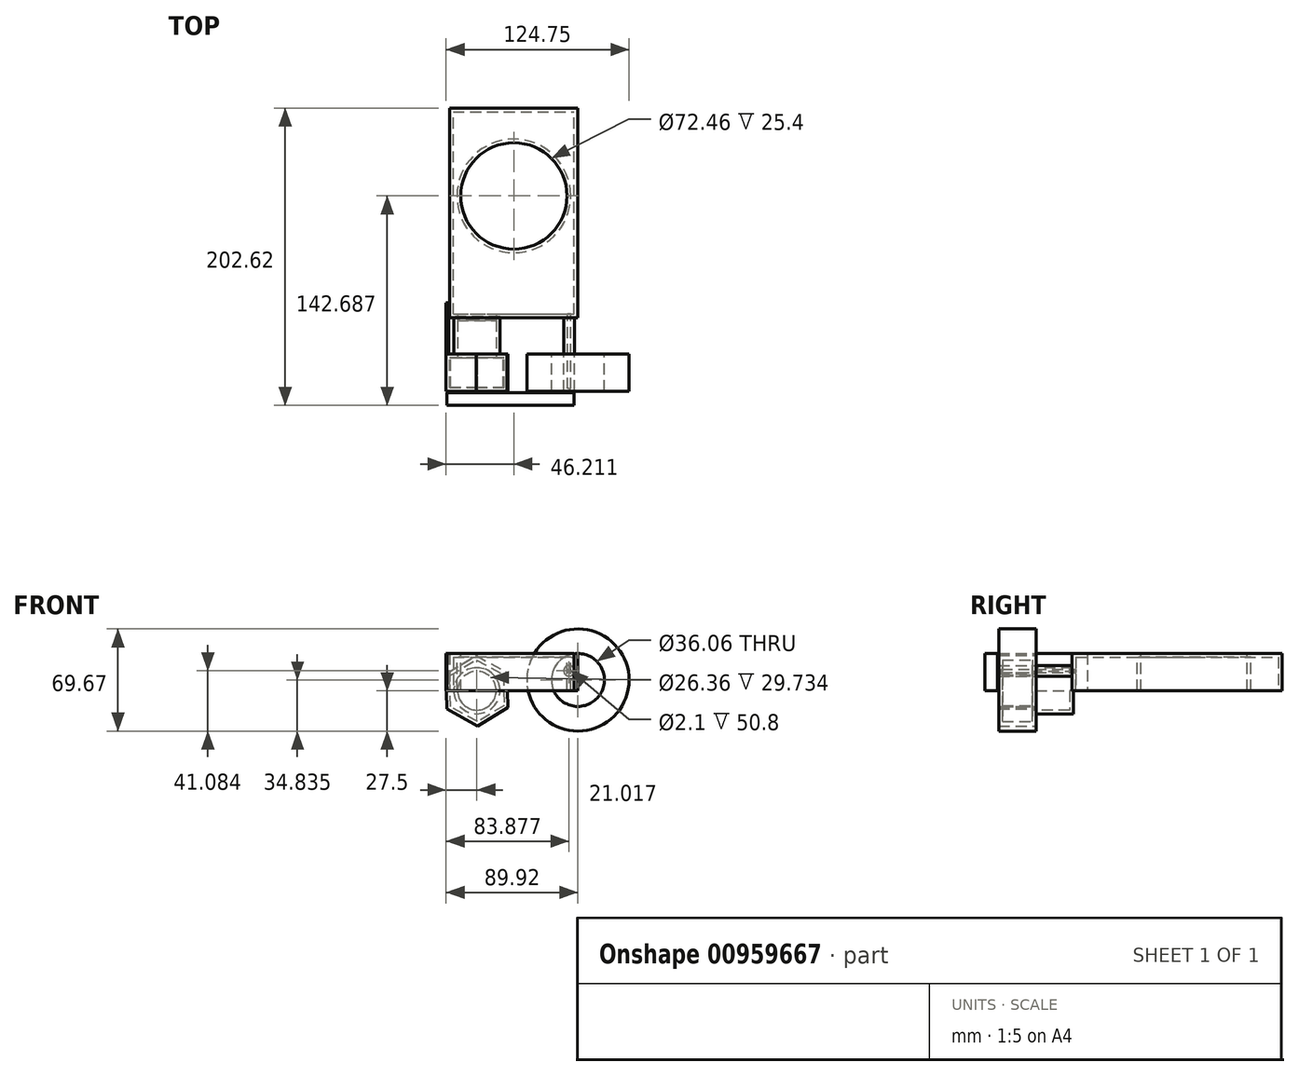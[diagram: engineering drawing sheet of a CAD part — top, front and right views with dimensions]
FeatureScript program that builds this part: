
annotation { "Feature Type Name" : "Feature", "Feature Type Description" : "" }
export const myFeature = defineFeature(function(context is Context, id is Id, definition is map)
    precondition{}
    {
        {
            var Q0;
            Q0=qCreatedBy(makeId("Front.planeOp"),FACE);
            var sketch = newSketch(context, id + "F0", { "sketchPlane" : qUnion([Q0])});
            skCircle(sketch, "E0.cCircle", {"center": v(-68.87, 0) * mm, "radius": 24 * mm, "construction": true});
            skLineSegment(sketch, "E0.0", {"start": v(-69.42, 23.98) * mm, "end": v(-48.38, 12.47) * mm});
            skLineSegment(sketch, "E0.1", {"start": v(-48.38, 12.47) * mm, "end": v(-47.83, -11.52) * mm});
            skLineSegment(sketch, "E0.2", {"start": v(-47.83, -11.52) * mm, "end": v(-68.32, -23.98) * mm});
            skLineSegment(sketch, "E0.3", {"start": v(-68.32, -23.98) * mm, "end": v(-89.37, -12.47) * mm});
            skLineSegment(sketch, "E0.4", {"start": v(-89.37, -12.47) * mm, "end": v(-89.92, 11.52) * mm});
            skLineSegment(sketch, "E0.5", {"start": v(-89.92, 11.52) * mm, "end": v(-69.42, 23.98) * mm});
            skSolve(sketch);
        }
        {
            var Q0;
            Q0=makeQuery(id+"F0.imprint","IMPRINT",FACE,{"disambiguationData":[TD([[makeQuery(id+"F0.imprint","IMPRINT",EDGE,{"derivedFrom":sQuery(id+"F0.wireOp",EDGE,"E0.0")}),-1.0]])]});
            extrude(context, id + "F1", {"entities" : qUnion([Q0]), "depth" : 25.4 * mm, "offsetDistance" : 25.4 * mm});
        }
        {
            var Q0;
            Q0=qCreatedBy(makeId("Front.planeOp"),FACE);
            var sketch = newSketch(context, id + "F2", { "sketchPlane" : qUnion([Q0])});
            skCircle(sketch, "E1", {"center": v(0, 0) * mm, "radius": 25.9 * mm});
            skCircle(sketch, "E2", {"center": v(0, 0) * mm, "radius": 17.2 * mm});
            skSolve(sketch);
        }
        {
            var Q0;
            Q0=makeQuery(id+"F2.imprint","IMPRINT",FACE,{"disambiguationData":[TD([[makeQuery(id+"F2.imprint","IMPRINT",EDGE,{"derivedFrom":sQuery(id+"F2.wireOp",EDGE,"E2")}),1.0]])]});
            var Q1;
            Q1=makeQuery(id+"F2.imprint","IMPRINT",FACE,{"disambiguationData":[TD([[makeQuery(id+"F2.imprint","IMPRINT",EDGE,{"derivedFrom":sQuery(id+"F2.wireOp",EDGE,"E1")}),1.0]])]});
            extrude(context, id + "F3", {"entities" : qUnion([Q0, Q1]), "operationType" : NewBodyOperationType.REMOVE, "oppositeDirection" : true, "depth" : 25.4 * mm, "offsetDistance" : 25.4 * mm});
        }
        {
            var Q0;
            Q0=qCreatedBy(makeId("Front.planeOp"),FACE);
            var sketch = newSketch(context, id + "F4", { "sketchPlane" : qUnion([Q0])});
            skCircle(sketch, "E3", {"center": v(0, 7.34) * mm, "radius": 34.83 * mm});
            skCircle(sketch, "E4", {"center": v(0, 7.34) * mm, "radius": 18.03 * mm});
            skSolve(sketch);
        }
        {
            var Q0;
            Q0 = qSketchRegion(id + "F4", true);
            extrude(context, id + "F5", {"entities" : qUnion([Q0]), "depth" : 25.4 * mm, "offsetDistance" : 25.4 * mm});
        }
        {
            var Q0;
            Q0=qCreatedBy(makeId("Front.planeOp"),FACE);
            var sketch = newSketch(context, id + "F6", { "sketchPlane" : qUnion([Q0])});
            skCircle(sketch, "E5", {"center": v(-68.46, 0) * mm, "radius": 14.96 * mm});
            skSolve(sketch);
        }
        {
            var Q0;
            Q0=makeQuery(id+"F6.imprint","IMPRINT",FACE,{"disambiguationData":[TD([[makeQuery(id+"F6.imprint","IMPRINT",EDGE,{"derivedFrom":sQuery(id+"F6.wireOp",EDGE,"E5")}),1.0]])]});
            extrude(context, id + "F7", {"entities" : qUnion([Q0]), "operationType" : NewBodyOperationType.ADD, "depth" : 25.4 * mm, "offsetDistance" : 25.4 * mm});
        }
        {
            var Q0;
            Q0=makeQuery(id+"F1.opExtrude","CAP_FACE",FACE,{"disambiguationData":[OSD([sQuery(id+"F0.wireOp",EDGE,"E0.0"),sQuery(id+"F0.wireOp",EDGE,"E0.1"),sQuery(id+"F0.wireOp",EDGE,"E0.2"),sQuery(id+"F0.wireOp",EDGE,"E0.3"),sQuery(id+"F0.wireOp",EDGE,"E0.4"),sQuery(id+"F0.wireOp",EDGE,"E0.5")])],"isStart":true});
            var sketch = newSketch(context, id + "F8", { "sketchPlane" : qUnion([Q0])});
            skCircle(sketch, "E6", {"center": v(68.9, 0) * mm, "radius": 15.72 * mm});
            skSolve(sketch);
        }
        {
            var Q0;
            Q0=makeQuery(id+"F8.imprint","IMPRINT",FACE,{"disambiguationData":[TD([[makeQuery(id+"F8.imprint","IMPRINT",EDGE,{"derivedFrom":sQuery(id+"F8.wireOp",EDGE,"E6")}),1.0]])]});
            extrude(context, id + "F9", {"entities" : qUnion([Q0]), "operationType" : NewBodyOperationType.ADD, "depth" : 25.4 * mm, "offsetDistance" : 25.4 * mm});
        }
        {
            var Q0;
            Q0=qCreatedBy(makeId("Top.planeOp"),FACE);
            var sketch = newSketch(context, id + "F10", { "sketchPlane" : qUnion([Q0])});
            skLineSegment(sketch, "E7.bottom", {"start": v(-87.54, 24.65) * mm, "end": v(0, 24.65) * mm});
            skLineSegment(sketch, "E7.top", {"start": v(-87.54, 38.16) * mm, "end": v(0, 38.16) * mm});
            skLineSegment(sketch, "E7.left", {"start": v(-87.54, 24.65) * mm, "end": v(-87.54, 38.16) * mm});
            skLineSegment(sketch, "E7.right", {"start": v(0, 24.65) * mm, "end": v(0, 38.16) * mm});
            skSolve(sketch);
        }
        {
            var Q0;
            Q0 = qSketchRegion(id + "F10", true);
            extrude(context, id + "F11", {"entities" : qUnion([Q0]), "operationType" : NewBodyOperationType.ADD, "depth" : 25.4 * mm, "offsetDistance" : 25.4 * mm});
        }
        {
            var Q0;
            Q0=makeQuery(id+"F11.opExtrude","SWEPT_FACE",FACE,{"disambiguationData":[OSD([sQuery(id+"F10.wireOp",EDGE,"E7.bottom")])]});
            var sketch = newSketch(context, id + "F12", { "sketchPlane" : qUnion([Q0])});
            skCircle(sketch, "E8", {"center": v(-6.04, 13.58) * mm, "radius": 3.59 * mm});
            skSolve(sketch);
        }
        {
            var Q0;
            Q0=makeQuery(id+"F12.imprint","IMPRINT",FACE,{"disambiguationData":[TD([[makeQuery(id+"F12.imprint","IMPRINT",EDGE,{"derivedFrom":sQuery(id+"F12.wireOp",EDGE,"E8")}),1.0]])]});
            extrude(context, id + "F13", {"entities" : qUnion([Q0]), "operationType" : NewBodyOperationType.ADD, "depth" : 25.4 * mm, "offsetDistance" : 25.4 * mm});
        }
        {
            var Q0;
            Q0=makeQuery(id+"F11.opExtrude","SWEPT_FACE",FACE,{"disambiguationData":[OSD([sQuery(id+"F10.wireOp",EDGE,"E7.top")])]});
            var sketch = newSketch(context, id + "F14", { "sketchPlane" : qUnion([Q0])});
            skLineSegment(sketch, "E9.bottom", {"start": v(87.54, 0) * mm, "end": v(49.94, 0) * mm});
            skLineSegment(sketch, "E9.top", {"start": v(87.54, -17.9) * mm, "end": v(49.94, -17.9) * mm});
            skLineSegment(sketch, "E9.left", {"start": v(87.54, 0) * mm, "end": v(87.54, -17.9) * mm});
            skLineSegment(sketch, "E9.right", {"start": v(49.94, 0) * mm, "end": v(49.94, -17.9) * mm});
            skSolve(sketch);
        }
        {
            var Q0;
            {var subQ3=sQuery(id+"F14.wireOp",EDGE,"E9.bottom");Q0=makeQuery(id+"F14.imprint","IMPRINT",FACE,{"disambiguationData":[TD([[makeQuery(id+"F14.imprint","IMPRINT",EDGE,{"derivedFrom":subQ3}),-1.0]])]});}
            extrude(context, id + "F15", {"entities" : qUnion([Q0]), "operationType" : NewBodyOperationType.ADD, "depth" : 129.54 * mm, "offsetDistance" : 25.4 * mm});
        }
        {
            var Q0;
            Q0=makeQuery(id+"F13.opExtrude","CAP_FACE",FACE,{"disambiguationData":[OSD([sQuery(id+"F12.wireOp",EDGE,"E8")])],"isStart":false});
            extrude(context, id + "F16", {"entities" : qUnion([Q0]), "operationType" : NewBodyOperationType.ADD, "depth" : 25.4 * mm, "offsetDistance" : 25.4 * mm});
        }
        {
            var Q0;
            Q0=qCreatedBy(makeId("Top.planeOp"),FACE);
            var sketch = newSketch(context, id + "F17", { "sketchPlane" : qUnion([Q0])});
            skLineSegment(sketch, "E10.bottom", {"start": v(-2.6, -26.22) * mm, "end": v(-2.6, -26.22) * mm});
            skLineSegment(sketch, "E10.top", {"start": v(-2.6, -25.99) * mm, "end": v(-2.6, -25.99) * mm});
            skLineSegment(sketch, "E10.left", {"start": v(-2.6, -26.22) * mm, "end": v(-2.6, -25.99) * mm});
            skLineSegment(sketch, "E10.right", {"start": v(-2.6, -26.22) * mm, "end": v(-2.6, -25.99) * mm});
            skLineSegment(sketch, "E11.bottom", {"start": v(-2.6, -26.22) * mm, "end": v(-89.4, -26.22) * mm});
            skLineSegment(sketch, "E11.top", {"start": v(-2.6, -34.92) * mm, "end": v(-89.4, -34.92) * mm});
            skLineSegment(sketch, "E11.left", {"start": v(-2.6, -26.22) * mm, "end": v(-2.6, -34.92) * mm});
            skLineSegment(sketch, "E11.right", {"start": v(-89.4, -26.22) * mm, "end": v(-89.4, -34.92) * mm});
            skSolve(sketch);
        }
        {
            var Q0;
            Q0 = qSketchRegion(id + "F17", true);
            extrude(context, id + "F18", {"entities" : qUnion([Q0]), "depth" : 25.4 * mm, "offsetDistance" : 25.4 * mm});
        }
        {
            var Q0;
            {var subQ0=sQuery(id+"F10.wireOp",EDGE,"E7.top");Q0=makeQuery(id+"F15.boolean.opBoolean","MERGE",FACE,{"derivedFrom":[makeQuery(id+"F11.opExtrude","CAP_FACE",FACE,{"disambiguationData":[OSD([sQuery(id+"F10.wireOp",EDGE,"E7.bottom"),subQ0,sQuery(id+"F10.wireOp",EDGE,"E7.left"),sQuery(id+"F10.wireOp",EDGE,"E7.right")])],"isStart":false}),makeQuery(id+"F15.opExtrude","SWEPT_FACE",FACE,{"disambiguationData":[OSD([subQ0])]})]});}
            var sketch = newSketch(context, id + "F19", { "sketchPlane" : qUnion([Q0])});
            skCircle(sketch, "E12", {"center": v(-43.7, 107.77) * mm, "radius": 36.23 * mm});
            skSolve(sketch);
        }
        {
            var Q0;
            Q0=makeQuery(id+"F19.imprint","IMPRINT",FACE,{"disambiguationData":[TD([[makeQuery(id+"F19.imprint","IMPRINT",EDGE,{"derivedFrom":sQuery(id+"F19.wireOp",EDGE,"E12")}),1.0]])]});
            var Q1;
            Q1 = qSketchRegion(id + "F19", true);
            extrude(context, id + "F20", {"entities" : qUnion([Q0, Q1]), "operationType" : NewBodyOperationType.REMOVE, "oppositeDirection" : true, "depth" : 25.4 * mm, "offsetDistance" : 25.4 * mm});
        }
        {
            var Q0;
            {var subQ0=sQuery(id+"F10.wireOp",EDGE,"E7.top");Q0=makeQuery(id+"F15.boolean.opBoolean","MERGE",FACE,{"derivedFrom":[makeQuery(id+"F11.opExtrude","CAP_FACE",FACE,{"disambiguationData":[OSD([sQuery(id+"F10.wireOp",EDGE,"E7.bottom"),subQ0,sQuery(id+"F10.wireOp",EDGE,"E7.left"),sQuery(id+"F10.wireOp",EDGE,"E7.right")])],"isStart":true}),makeQuery(id+"F15.opExtrude","SWEPT_FACE",FACE,{"disambiguationData":[OSD([subQ0,sQuery(id+"F14.wireOp",EDGE,"E9.bottom")])]})]});}
            shell(context, id + "F21", {"entities" : qUnion([Q0]), "thickness" : 2.54 * mm});
        }
        {
            var Q0;
            Q0=qCreatedBy(makeId("Top.planeOp"),FACE);
            var sketch = newSketch(context, id + "F22", { "sketchPlane" : qUnion([Q0])});
            skLineSegment(sketch, "E13.bottom", {"start": v(-89.83, 0) * mm, "end": v(-88.02, 0) * mm});
            skLineSegment(sketch, "E13.top", {"start": v(-89.83, 34.97) * mm, "end": v(-88.02, 34.97) * mm});
            skLineSegment(sketch, "E13.left", {"start": v(-88.02, 0) * mm, "end": v(-88.02, 34.97) * mm});
            skLineSegment(sketch, "E13.right", {"start": v(-89.83, 0) * mm, "end": v(-89.83, 34.97) * mm});
            skSolve(sketch);
        }
        {
            var Q0;
            Q0 = qSketchRegion(id + "F22", true);
            extrude(context, id + "F23", {"entities" : qUnion([Q0]), "operationType" : NewBodyOperationType.ADD, "depth" : 25.4 * mm, "offsetDistance" : 25.4 * mm});
        }
    });
